# Revit family: LUXI_PANEL LIGHT_LG-E
name_source: partatom
category: Apparecchi per illuminazione
revit_build: Autodesk Revit 2016 (Build: 20161004_0715(x64)
units: mm (PartAtom-declared; Revit-internal decimal feet)

## family parameters
Condiviso = No
Host = Superficie
Numero OmniClass = 23.80.70.00
Punto di calcolo locali = Sì
Quota connettore circolare = Usa diametro
Sorgente d'illuminazione = Sì
Taglio con vuoti quando caricato = No
Tipo di parte = Normale
Titolo OmniClass = Lighting

## types (2) — shared parameters
Alimentatore = Incluso, dimmerabile
Alimentazione = 220-240V AC / 50-60 Hz
Angolo inclinazione = -90.00°
Carico apparente = 36 VA
Certificazioni = CE / RohS
Classe di efficienza energetica = A++
Classe di protezione = II
Classe di rischio fotobiologico = Esente (RG0)
Colore = Bianco
Descrizione = LED panel ad alta efficienza
Fattore di correzione di potenza = ≥0,95 (typ.)
Filtro dei colori = 16777215
Garanzia = 5 anni
Grado di protezione = IP20, IP 44 (frontale)
H = 11 mm  [stored 0.0360892 ft]
IFCExportAs = IFCLightFixtureType
Indice di resa cromatica = ≥90 (typ.)
Masterformat 2016 Codice = 26.50.00
Masterformat 2016 Descrizione = Lighting
Materiale 1 = Tecnopolimero Microprismatico Alta Trasmittanza
Materiale 2 = Alluminio Estruso_Bianco
Materiale 3 = Lamiera Acciaio
Modello = Serie LG-E | Panel Light
OFF1 = 38 mm  [stored 0.124672 ft]
Ottiche = Pannello microprismatico UGR≤19
Potenza = 36 W
Produttore = Luxi Illuminazione S.r.l.
Prospetto di default = 2000 mm  [stored 6.56168 ft]
Protezione agli urti = IK07 (2 Joule)
Regolazione del flusso luminoso = 1-10V / DALI / PUSH DIM selezionabile da dip-switch
Rendi la forma visibile nel rendering = No
Revisione = 3
Sistema di illuminazione = Luce indiretta (edge light)
Sorgente = LED SMD
Step MacAdam (SDCM) = <4
Temperatura di esercizio = 0°C / +40°C
Tipologie di installazione = Incasso / plafone / sospensione
URL = https://www.luxi.lighting
Uniclass 2015 Codice = EF_70_80
Uniclass 2015 Descrizione = Lighting
Variazione temperatura colore lampada con luminosità attenuata = <Nessuno>
Vita utile = L70B20 60.000ore

## per-type parameters (varying)
| type | Dimensioni | Emetti da larghezza rettangolo | Emetti da lunghezza rettangolo | File diagramma fotometrico | Larghezza | Lunghezza | Peso |
| LPGE036660W940DA | 595x595x11 | 519 mm  [stored 1.70276 ft] | 519 mm  [stored 1.70276 ft] | LPGE036660W940DA Luxi SERIE LG-E CRI90 DIM 60x60 36W 4000K.IES | 595 mm  [stored 1.9521 ft] | 595 mm  [stored 1.9521 ft] | 3.60 kg |
| LPGE036312W940DA | 295x1295x11 | 219 mm | 1119 mm  [stored 3.67126 ft] | LPGE036312W940DA Luxi SERIE LG-E CRI90 DIM 30x120 36W 4000K.IES | 295 mm  [stored 0.967848 ft] | 1195 mm  [stored 3.9206 ft] | 3.80 kg |

note: column(s) folded — value = type name in every type: Articolo

note: [stored X ft] marks values corroborated as IEEE doubles in the binary element streams (Revit-internal decimal feet)
